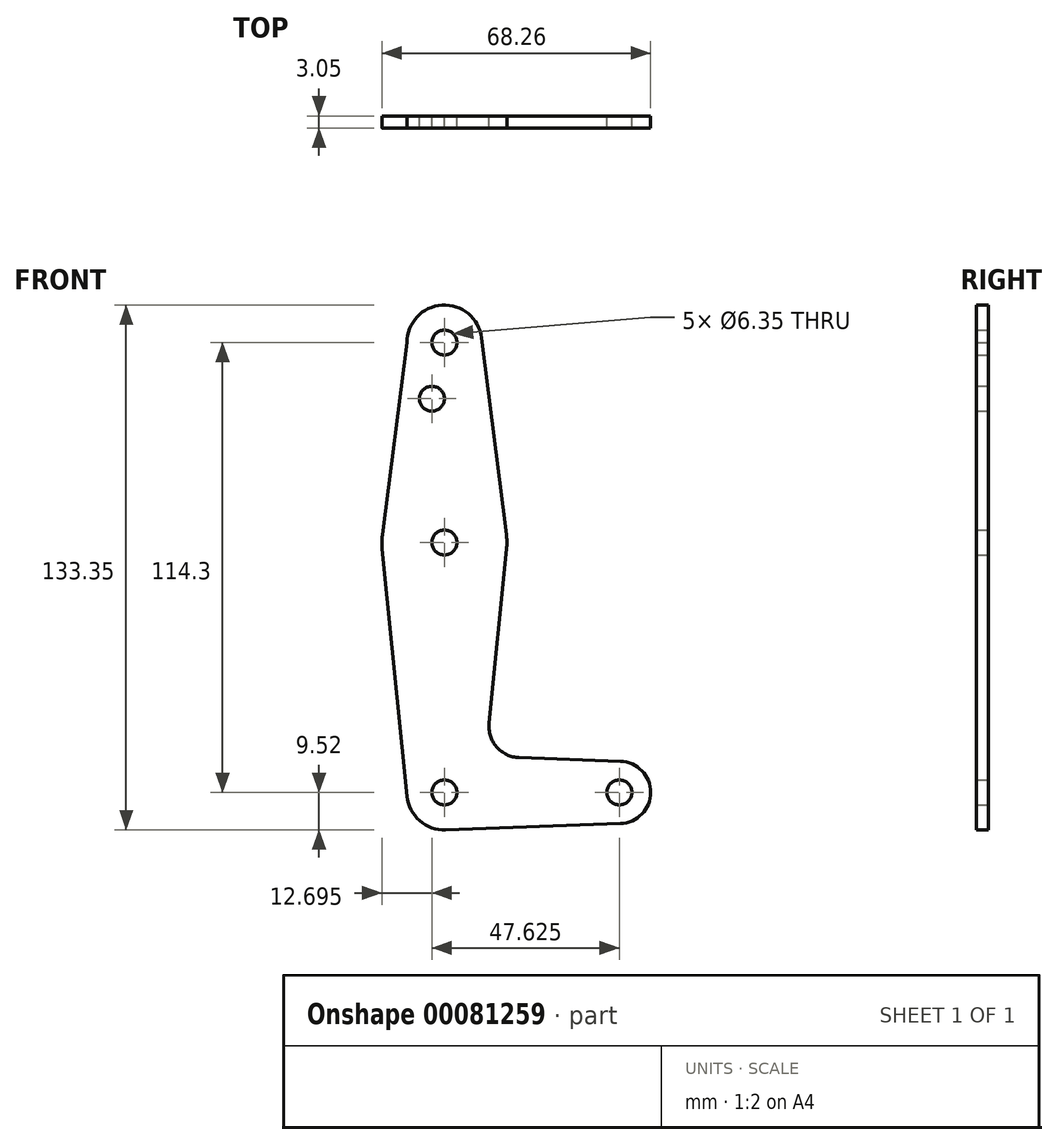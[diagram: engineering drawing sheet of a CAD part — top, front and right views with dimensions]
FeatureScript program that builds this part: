
annotation { "Feature Type Name" : "Feature", "Feature Type Description" : "" }
export const myFeature = defineFeature(function(context is Context, id is Id, definition is map)
    precondition{}
    {
        {
            var Q0;
            Q0=qCreatedBy(makeId("Front.planeOp"),FACE);
            var sketch = newSketch(context, id + "F0", { "sketchPlane" : qUnion([Q0])});
            skCircle(sketch, "E0", {"center": v(0, 0) * mm, "radius": 9.53 * mm});
            skCircle(sketch, "E1", {"center": v(0, 63.5) * mm, "radius": 15.88 * mm});
            skCircle(sketch, "E2", {"center": v(0, 114.3) * mm, "radius": 9.53 * mm});
            skCircle(sketch, "E3", {"center": v(44.45, 0) * mm, "radius": 7.94 * mm});
            skLineSegment(sketch, "E4", {"start": v(0, 0) * mm, "end": v(0, 114.3) * mm, "construction": true});
            skLineSegment(sketch, "E5", {"start": v(0, 0) * mm, "end": v(44.45, 0) * mm, "construction": true});
            skLineSegment(sketch, "E6", {"start": v(-9.53, 114.3) * mm, "end": v(-15.75, 65.5) * mm});
            skLineSegment(sketch, "E7", {"start": v(9.45, 115.5) * mm, "end": v(15.75, 65.48) * mm});
            skCircle(sketch, "E8", {"center": v(0, 114.3) * mm, "radius": 3.18 * mm});
            skCircle(sketch, "E9", {"center": v(0, 63.5) * mm, "radius": 3.18 * mm});
            skCircle(sketch, "E10", {"center": v(0, 0) * mm, "radius": 3.18 * mm});
            skCircle(sketch, "E11", {"center": v(44.45, 0) * mm, "radius": 3.18 * mm});
            skCircle(sketch, "E12", {"center": v(-3.18, 100.03) * mm, "radius": 3.18 * mm});
            skPoint(sketch, "E13.newPointA", {"position": v(9.57, 0) * mm});
            skPoint(sketch, "E13.newPointB", {"position": v(0, 9.53) * mm});
            skLineSegment(sketch, "E14", {"start": v(-15.8, 61.91) * mm, "end": v(-9.48, -0.95) * mm});
            skLineSegment(sketch, "E15", {"start": v(15.8, 61.91) * mm, "end": v(11.34, 17.6) * mm});
            skLineSegment(sketch, "E16", {"start": v(18.97, 8.85) * mm, "end": v(44.73, 7.93) * mm});
            skLineSegment(sketch, "E17", {"start": v(0.34, -9.52) * mm, "end": v(44.73, -7.93) * mm});
            skArc(sketch, "E18.filletArc", {"start": v(11.34, 17.6) * mm, "mid": v(13.26, 11.57) * mm, "end": v(18.97, 8.85) * mm});
            skSolve(sketch);
        }
        {
            var Q0;
            {var subQ1=sQuery(id+"F0.wireOp",EDGE,"E6");Q0=makeQuery(id+"F0.imprint","IMPRINT",FACE,{"disambiguationData":[TD([[makeQuery(id+"F0.imprint","IMPRINT",EDGE,{"derivedFrom":subQ1}),1.0]])]});}
            var Q1;
            Q1=makeQuery(id+"F0.imprint","IMPRINT",FACE,{"disambiguationData":[TD([[makeQuery(id+"F0.imprint","IMPRINT",EDGE,{"derivedFrom":sQuery(id+"F0.wireOp",EDGE,"E8")}),-1.0]])]});
            var Q2;
            {var subQ3=sQuery(id+"F0.wireOp",EDGE,"E14");Q2=makeQuery(id+"F0.imprint","IMPRINT",FACE,{"disambiguationData":[TD([[makeQuery(id+"F0.imprint","IMPRINT",EDGE,{"derivedFrom":subQ3}),1.0]])]});}
            var Q3;
            Q3=makeQuery(id+"F0.imprint","IMPRINT",FACE,{"disambiguationData":[TD([[makeQuery(id+"F0.imprint","IMPRINT",EDGE,{"derivedFrom":sQuery(id+"F0.wireOp",EDGE,"E9")}),-1.0]])]});
            var Q4;
            Q4=makeQuery(id+"F0.imprint","IMPRINT",FACE,{"disambiguationData":[TD([[makeQuery(id+"F0.imprint","IMPRINT",EDGE,{"derivedFrom":sQuery(id+"F0.wireOp",EDGE,"E10")}),-1.0]])]});
            var Q5;
            Q5=makeQuery(id+"F0.imprint","IMPRINT",FACE,{"disambiguationData":[TD([[makeQuery(id+"F0.imprint","IMPRINT",EDGE,{"derivedFrom":sQuery(id+"F0.wireOp",EDGE,"E11")}),-1.0]])]});
            extrude(context, id + "F1", {"entities" : qUnion([Q0, Q1, Q2, Q3, Q4, Q5]), "depth" : 3.05 * mm});
        }
    });
